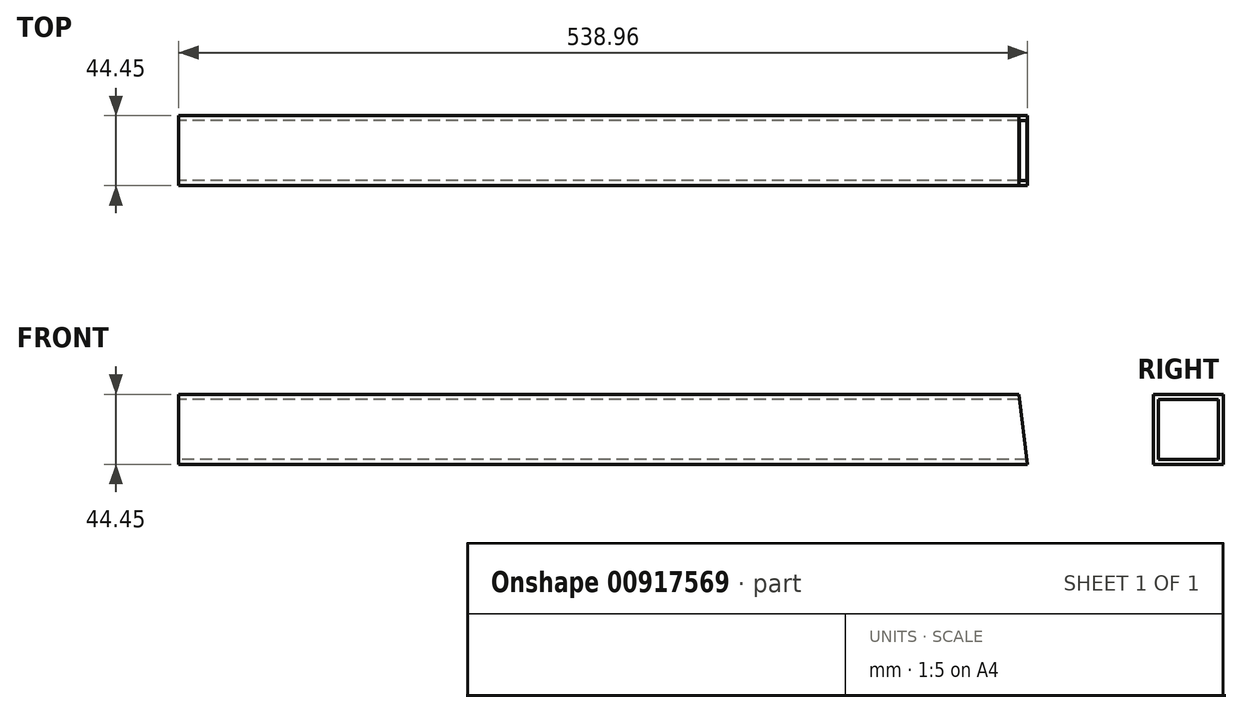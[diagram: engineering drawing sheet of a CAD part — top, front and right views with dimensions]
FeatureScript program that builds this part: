
annotation { "Feature Type Name" : "Feature", "Feature Type Description" : "" }
export const myFeature = defineFeature(function(context is Context, id is Id, definition is map)
    precondition{}
    {
        {
            var Q0;
            Q0=qCreatedBy(makeId("Front.planeOp"),FACE);
            var sketch = newSketch(context, id + "F0", { "sketchPlane" : qUnion([Q0])});
            skLineSegment(sketch, "E0", {"start": v(0, 0) * mm, "end": v(0, 44.45) * mm});
            skLineSegment(sketch, "E1", {"start": v(0, 44.45) * mm, "end": v(533.4, 44.45) * mm});
            skLineSegment(sketch, "E2", {"start": v(533.4, 44.45) * mm, "end": v(538.96, 0) * mm});
            skLineSegment(sketch, "E3", {"start": v(538.96, 0) * mm, "end": v(0, 0) * mm});
            skSolve(sketch);
        }
        {
            var Q0;
            Q0=makeQuery(id+"F0.imprint","IMPRINT",FACE,{"disambiguationData":[TD([[makeQuery(id+"F0.imprint","IMPRINT",EDGE,{"derivedFrom":sQuery(id+"F0.wireOp",EDGE,"E0")}),-1.0]])]});
            extrude(context, id + "F1", {"entities" : qUnion([Q0]), "depth" : 44.45 * mm, "offsetDistance" : 25.4 * mm});
        }
        {
            var Q0;
            Q0=makeQuery(id+"F1.opExtrude","SWEPT_FACE",FACE,{"disambiguationData":[OSD([sQuery(id+"F0.wireOp",EDGE,"E0")])]});
            var sketch = newSketch(context, id + "F2", { "sketchPlane" : qUnion([Q0])});
            skLineSegment(sketch, "E4.0", {"start": v(3.18, 41.28) * mm, "end": v(3.18, 3.18) * mm});
            skLineSegment(sketch, "E4.1", {"start": v(41.28, 41.28) * mm, "end": v(3.17, 41.28) * mm});
            skLineSegment(sketch, "E4.2", {"start": v(41.28, 3.18) * mm, "end": v(41.28, 41.28) * mm});
            skLineSegment(sketch, "E4.3", {"start": v(3.17, 3.18) * mm, "end": v(41.28, 3.18) * mm});
            skSolve(sketch);
        }
        {
            var Q0;
            Q0=makeQuery(id+"F2.imprint","IMPRINT",FACE,{"disambiguationData":[TD([[makeQuery(id+"F2.imprint","IMPRINT",EDGE,{"derivedFrom":sQuery(id+"F2.wireOp",EDGE,"E4.0")}),1.0]])]});
            extrude(context, id + "F3", {"entities" : qUnion([Q0]), "operationType" : NewBodyOperationType.REMOVE, "endBound" : BoundingType.THROUGH_ALL, "oppositeDirection" : true, "depth" : 25.4 * mm, "offsetDistance" : 25.4 * mm});
        }
    });
